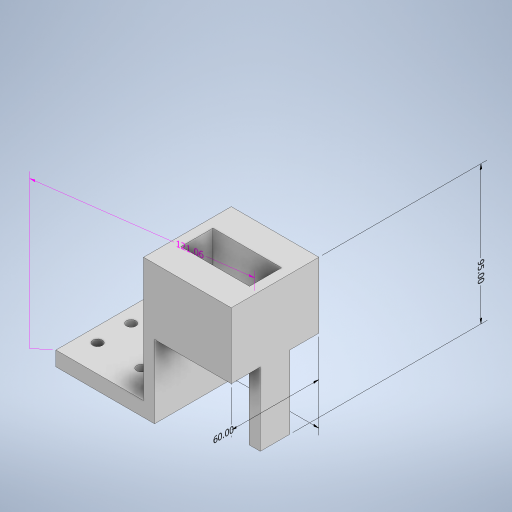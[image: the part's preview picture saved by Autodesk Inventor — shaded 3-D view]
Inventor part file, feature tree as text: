
AUTODESK INVENTOR PART (.ipt)
format: ipt  version: 2023 (Build 270158000, 158)  size: 355,328 bytes
history: native  units: mm
features: extrude x8, sketch x8, other x6, plane x1
ambient origin geometry x8: Origin, YZ Plane, XZ Plane, XY Plane, X Axis, Y Axis, Z Axis, Center Point
bodies: Body1 (feature_tree)
feature tree (23):
  other  "Sólido1"
  other  "Anotaciones"
  extrude  "Extrusión1"  Depth=60.0mm
  extrude  "Extrusión2"  Depth=45.0mm
  extrude  "Extrusión4"  TaperAngle=0.0deg  [1 undecoded]
  extrude  "Extrusión5"  Depth=30.0mm
  extrude  "Extrusión6"  Depth=60.0mm
  extrude  "Extrusión7"  Depth=20.0mm
  plane  "Plano de trabajo1"
  extrude  "Extrusión8"  Depth=18.5mm
  extrude  "Extrusión9"  Depth=30.0mm
  sketch  "Boceto2"  dims[d0=60.0mm d1=60.0mm]
  sketch  "Boceto3"  dims[d2=55.0mm d3=0.0mm d4=45.0mm]
  sketch  "Boceto5"  dims[d5=50.0mm d6=0.0mm]
  sketch  "Boceto6"  dims[d7=190.0mm d8=0.0mm d16=30.0mm]
  sketch  "Boceto7"  dims[d17=60.0mm d18=60.0mm]
  sketch  "Boceto8"  dims[d19=6.5mm d20=20.0mm]
  sketch  "Boceto10"  dims[d21=18.5mm d22=23.0mm]
  sketch  "Boceto11"  dims[d23=6.5mm d24=30.0mm d25=18.5mm d26=10.0mm d27=0.0mm d28=60.0mm d29=40.0mm d30=0.0mm d31=47.0mm d32=22.0mm d33=43.0mm d34=0.0mm d35=22.0mm d36=10.0mm d37=0.0mm d38=10.0mm d39=0.0mm d41=0.0mm d42=15.0mm d43=0.0mm d53=3.0mm d54=3.0mm d55=20.0mm d56=10.0mm d57=0.0mm d13=0.760408mm d14=1.168497mm d15=60.0mm d44=2.330497mm d45=4.198531mm d46=60.0mm d47=6.03005mm d48=2.762466mm d49=121.061968mm d50=5.581744mm d51=5.983744mm d52=95.0mm]
  other  "Cota lineal 1"
  other  "Cota lineal 2"
  other  "Cota lineal 3"
  other  "Cota lineal 4"
note: 1 required parameter value undecoded (feature->parameter linkage not recoverable at this tier; creation-order binding heuristic only, values carry confidence <= 0.55)
